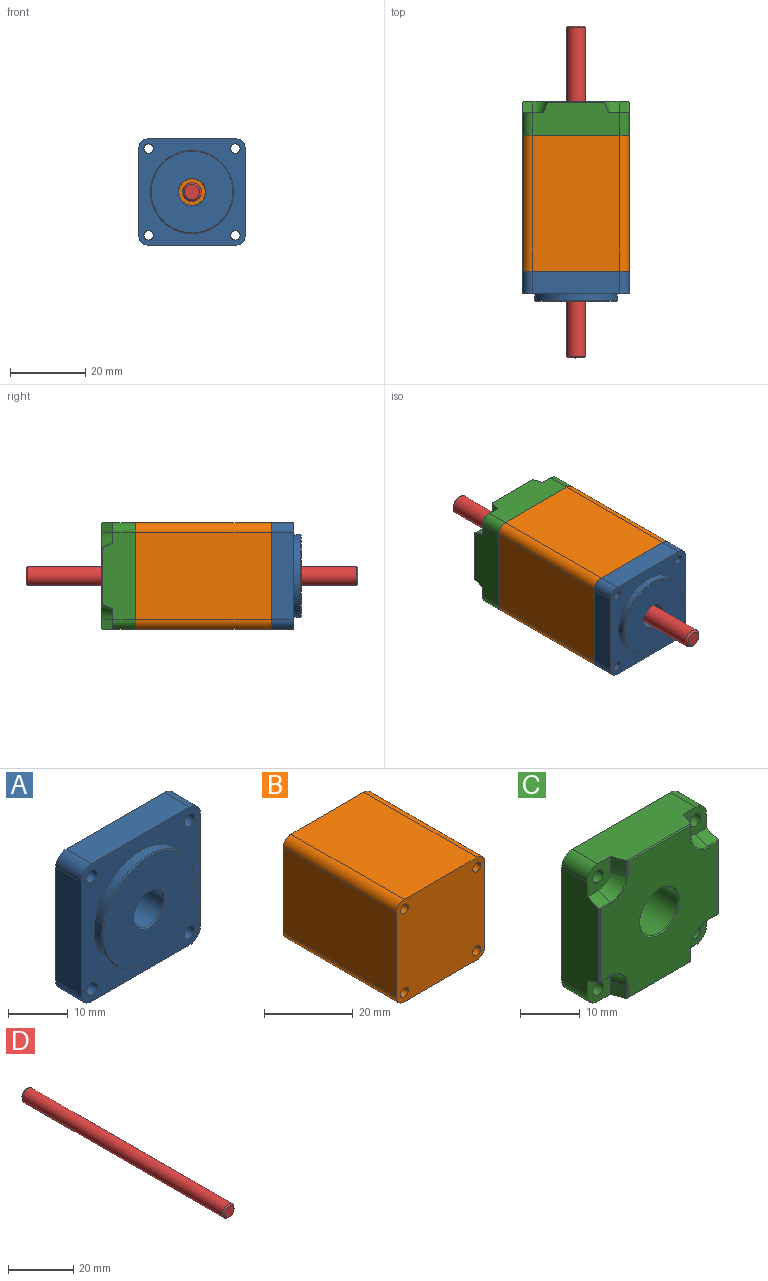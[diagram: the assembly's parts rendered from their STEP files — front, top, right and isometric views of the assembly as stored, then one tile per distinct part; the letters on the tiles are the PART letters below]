
ASSEMBLY  parts=4 mates=3
PART A: 19 faces, bbox 28.2x8x28.2 mm
  f0: plane 23.2x6mm, normal (-1,0,0), area 139.2mm2, adj f4,f5,f15,f18
  f1: plane 23.2x6mm, normal (0,0,-1), area 139.2mm2, adj f4,f5,f15,f16
  f2: plane 23.2x6mm, normal (1,0,0), area 139.2mm2, adj f4,f5,f16,f17
  f3: plane 23.2x6mm, normal (0,0,1), area 139.2mm2, adj f4,f5,f17,f18
  f4: plane 28.2x28.2mm, normal (0,-1,0), area 390.1mm2, adj f0,f1,f2,f3,f6,f9,f10,f11
  f5: plane 28.2x28.2mm, normal (0,1,0), area 731.8mm2, adj f0,f1,f2,f3,f8,f9,f10,f11
  f6: cylinder r=11mm len=22mm, axis (0,1,0), area 124.4mm2, adj f4,f14
  f7: plane 21.6x21.6mm, normal (0,-1,0), area 323.4mm2, adj f13,f14
  f8: cylinder r=3.5mm len=7.8mm, axis (0,-1,0), area 171.5mm2, adj f5,f13
  f9: cylinder r=1.25mm len=6mm, axis (0,-1,0), area 47.1mm2, adj f4,f5
  f10: cylinder r=1.25mm len=6mm, axis (0,-1,0), area 47.1mm2, adj f4,f5
  f11: cylinder r=1.25mm len=6mm, axis (0,-1,0), area 47.1mm2, adj f4,f5
  f12: cylinder r=1.25mm len=6mm, axis (0,-1,0), area 47.1mm2, adj f4,f5
  f13: cone r=3.5mm half-angle=45deg, axis (0,-1,0), area 6.4mm2, adj f7,f8
  f14: cone r=10.8mm half-angle=45deg, axis (0,1,0), area 19.4mm2, adj f6,f7
  f15: cylinder r=2.5mm len=6mm, axis (0,1,0), area 23.6mm2, adj f0,f1,f4,f5
  f16: cylinder r=2.5mm len=6mm, axis (0,-1,0), area 23.6mm2, adj f1,f2,f4,f5
  f17: cylinder r=2.5mm len=6mm, axis (0,1,0), area 23.6mm2, adj f2,f3,f4,f5
  f18: cylinder r=2.5mm len=6mm, axis (0,-1,0), area 23.6mm2, adj f0,f3,f4,f5
PART B: 14 faces, bbox 28.2x36x28.2 mm
  f0: plane 36x23.2mm, normal (-1,0,0), area 835.2mm2, adj f4,f5,f10,f13
  f1: plane 36x23.2mm, normal (0,0,-1), area 835.2mm2, adj f4,f5,f10,f11
  f2: plane 36x23.2mm, normal (1,0,0), area 835.2mm2, adj f4,f5,f11,f12
  f3: plane 36x23.2mm, normal (0,0,1), area 835.2mm2, adj f4,f5,f12,f13
  f4: plane 28.2x28.2mm, normal (0,-1,0), area 770.2mm2, adj f0,f1,f2,f3,f6,f7,f8,f9
  f5: plane 28.2x28.2mm, normal (0,1,0), area 770.2mm2, adj f0,f1,f2,f3,f6,f7,f8,f9
  f6: cylinder r=1.25mm len=36mm, axis (0,-1,0), area 282.7mm2, adj f4,f5
  f7: cylinder r=1.25mm len=36mm, axis (0,-1,0), area 282.7mm2, adj f4,f5
  f8: cylinder r=1.25mm len=36mm, axis (0,-1,0), area 282.7mm2, adj f4,f5
  f9: cylinder r=1.25mm len=36mm, axis (0,-1,0), area 282.7mm2, adj f4,f5
  f10: cylinder r=2.5mm len=36mm, axis (0,1,0), area 141.4mm2, adj f0,f1,f4,f5
  f11: cylinder r=2.5mm len=36mm, axis (0,-1,0), area 141.4mm2, adj f1,f2,f4,f5
  f12: cylinder r=2.5mm len=36mm, axis (0,1,0), area 141.4mm2, adj f2,f3,f4,f5
  f13: cylinder r=2.5mm len=36mm, axis (0,-1,0), area 141.4mm2, adj f0,f3,f4,f5
PART C: 48 faces, bbox 28.2x9x28.2 mm
  f0: plane 23.2x8.8mm, normal (-1,0,0), area 184.5mm2, adj f9,f13,f14,f15,f26,f27,f30,f31
  f1: plane 23.2x8.8mm, normal (0,0,-1), area 184.5mm2, adj f9,f12,f13,f17,f18,f27,f28,f39
  f2: plane 23.2x8.8mm, normal (1,0,0), area 184.5mm2, adj f9,f11,f12,f20,f21,f28,f29,f46
  f3: plane 23.2x8.8mm, normal (0,0,1), area 184.5mm2, adj f9,f11,f14,f23,f24,f29,f30,f38
  f4: plane 27.8x27.8mm, normal (0,-1,0), area 547.4mm2, adj f31,f32,f33,f34,f35,f36,f37,f38
  f5: cylinder r=1.25mm len=6mm, axis (0,-1,0), area 47.1mm2, adj f9,f14
  f6: cylinder r=1.25mm len=6mm, axis (0,-1,0), area 47.1mm2, adj f9,f13
  f7: cylinder r=1.25mm len=6mm, axis (0,-1,0), area 47.1mm2, adj f9,f12
  f8: cylinder r=1.25mm len=6mm, axis (0,-1,0), area 47.1mm2, adj f9,f11
  f9: plane 28.2x28.2mm, normal (0,1,0), area 706.6mm2, adj f0,f1,f2,f3,f5,f6,f7,f8
  f10: cylinder r=4.5mm len=9mm, axis (0,-1,0), area 248.8mm2, adj f9,f47
  f11: plane 5.5x5.5mm, normal (0,-1,0), area 22.2mm2, adj f2,f3,f8,f21,f22,f23,f29
  f12: plane 5.5x5.5mm, normal (0,-1,0), area 22.2mm2, adj f1,f2,f7,f18,f19,f20,f28
  f13: plane 5.5x5.5mm, normal (0,-1,0), area 22.2mm2, adj f0,f1,f6,f15,f16,f17,f27
  f14: plane 5.5x5.5mm, normal (0,-1,0), area 22.2mm2, adj f0,f3,f5,f24,f25,f26,f30
  f15: plane 2.87x2.6mm, normal (0,-0.34,-0.94), area 7.9mm2, adj f0,f13,f16,f31,f33
  f16: cone r=2.9mm half-angle=20deg, axis (0,-1,0), area 16.4mm2, adj f13,f15,f17,f35
  f17: plane 2.87x2.6mm, normal (-0.94,-0.34,0), area 7.9mm2, adj f1,f13,f16,f37,f39
  f18: plane 2.87x2.6mm, normal (0.94,-0.34,0), area 7.9mm2, adj f1,f12,f19,f39,f41
  f19: cone r=2.9mm half-angle=20deg, axis (0,-1,0), area 16.4mm2, adj f12,f18,f20,f43
  f20: plane 2.87x2.6mm, normal (0,-0.34,-0.94), area 7.9mm2, adj f2,f12,f19,f45,f46
  f21: plane 2.87x2.6mm, normal (0,-0.34,0.94), area 7.9mm2, adj f2,f11,f22,f44,f46
  f22: cone r=2.9mm half-angle=20deg, axis (0,-1,0), area 16.4mm2, adj f11,f21,f23,f42
  f23: plane 2.87x2.6mm, normal (0.94,-0.34,0), area 7.9mm2, adj f3,f11,f22,f38,f40
  f24: plane 2.87x2.6mm, normal (-0.94,-0.34,0), area 7.9mm2, adj f3,f14,f25,f36,f38
  f25: cone r=2.9mm half-angle=20deg, axis (0,-1,0), area 16.4mm2, adj f14,f24,f26,f34
  f26: plane 2.87x2.6mm, normal (0,-0.34,0.94), area 7.9mm2, adj f0,f14,f25,f31,f32
  f27: cylinder r=2.5mm len=6mm, axis (0,1,0), area 23.6mm2, adj f0,f1,f9,f13
  f28: cylinder r=2.5mm len=6mm, axis (0,-1,0), area 23.6mm2, adj f1,f2,f9,f12
  f29: cylinder r=2.5mm len=6mm, axis (0,1,0), area 23.6mm2, adj f2,f3,f9,f11
  f30: cylinder r=2.5mm len=6mm, axis (0,-1,0), area 23.6mm2, adj f0,f3,f9,f14
  f31: plane 15.16x0.2mm, normal (-0.71,-0.71,0), area 4.2mm2, adj f0,f4,f15,f26,f32,f33
  f32: plane 2.53x0.19mm, normal (0,-0.82,0.57), area 0.6mm2, adj f4,f26,f31,f34
  f33: plane 2.53x0.19mm, normal (0,-0.82,-0.57), area 0.6mm2, adj f4,f15,f31,f35
  f34: cone r=4.13mm half-angle=55deg, axis (0,-1,0), area 1.5mm2, adj f4,f25,f32,f36
  f35: cone r=4.13mm half-angle=55deg, axis (0,-1,0), area 1.5mm2, adj f4,f16,f33,f37
  f36: plane 2.53x0.19mm, normal (-0.57,-0.82,0), area 0.6mm2, adj f4,f24,f34,f38
  f37: plane 2.53x0.19mm, normal (-0.57,-0.82,0), area 0.6mm2, adj f4,f17,f35,f39
  f38: plane 15.16x0.2mm, normal (0,-0.71,0.71), area 4.2mm2, adj f3,f4,f23,f24,f36,f40
  f39: plane 15.16x0.2mm, normal (0,-0.71,-0.71), area 4.2mm2, adj f1,f4,f17,f18,f37,f41
  f40: plane 2.53x0.19mm, normal (0.57,-0.82,0), area 0.6mm2, adj f4,f23,f38,f42
  f41: plane 2.53x0.19mm, normal (0.57,-0.82,0), area 0.6mm2, adj f4,f18,f39,f43
  f42: cone r=4.13mm half-angle=55deg, axis (0,-1,0), area 1.5mm2, adj f4,f22,f40,f44
  f43: cone r=4.13mm half-angle=55deg, axis (0,-1,0), area 1.5mm2, adj f4,f19,f41,f45
  f44: plane 2.53x0.19mm, normal (0,-0.82,0.57), area 0.6mm2, adj f4,f21,f42,f46
  f45: plane 2.53x0.19mm, normal (0,-0.82,-0.57), area 0.6mm2, adj f4,f20,f43,f46
  f46: plane 15.16x0.2mm, normal (0.71,-0.71,0), area 4.2mm2, adj f2,f4,f20,f21,f44,f45
  f47: cone r=4.5mm half-angle=45deg, axis (0,-1,0), area 8.2mm2, adj f4,f10
PART D: 5 faces, bbox 5x88x5 mm
  f0: cylinder r=2.5mm len=87mm, axis (0,1,0), area 1366.6mm2, adj f3,f4
  f1: plane 4x4mm, normal (0,-1,0), area 12.6mm2, adj f4
  f2: plane 4x4mm, normal (0,1,0), area 12.6mm2, adj f3
  f3: cone r=2.5mm half-angle=45deg, axis (0,-1,0), area 10mm2, adj f0,f2
  f4: cone r=2mm half-angle=45deg, axis (0,1,0), area 10mm2, adj f0,f1
PLACE A t=(0.16,1.48,0.58)mm fixed
PLACE B t=(0.16,22.48,0.58)mm
PLACE C rot(axis=(0,0,1),180deg) t=(0.16,44.98,0.58)mm
PLACE D t=(0.16,69.48,0.58)mm
MATE fastened B.f6 <-> A.f9  axis (0,-1,0) through (-11.34,4.48,12.08)mm
MATE revolute D.f0 <-> A.f6  axis (0,-1,0) through (0.16,-18.52,0.58)mm
MATE fastened C.f30 <-> B.f12  axis (0,-1,0) through (11.76,40.48,12.18)mm
